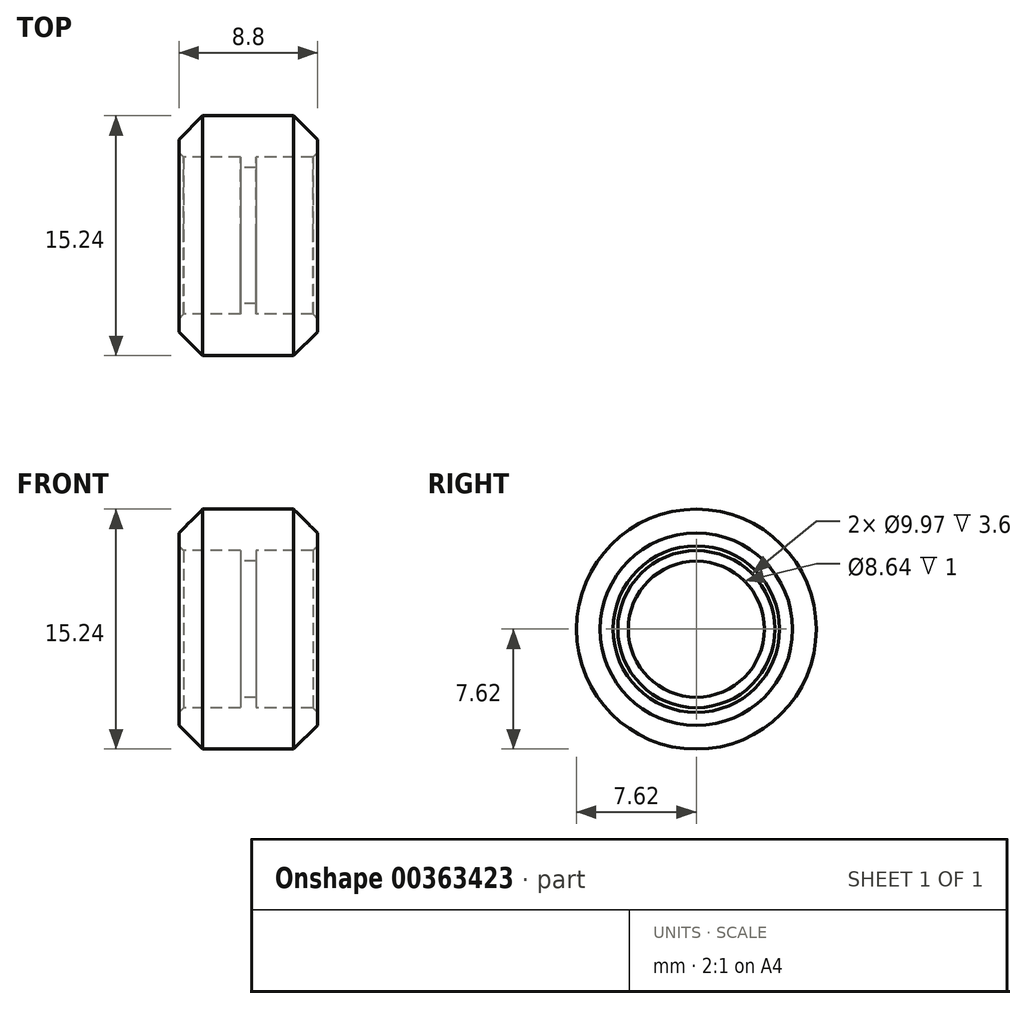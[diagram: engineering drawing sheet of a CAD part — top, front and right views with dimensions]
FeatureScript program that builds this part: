
annotation { "Feature Type Name" : "Feature", "Feature Type Description" : "" }
export const myFeature = defineFeature(function(context is Context, id is Id, definition is map)
    precondition{}
    {
        {
            var Q0;
            Q0=qCreatedBy(makeId("Front.planeOp"),FACE);
            var sketch = newSketch(context, id + "F0", { "sketchPlane" : qUnion([Q0])});
            skLineSegment(sketch, "E0", {"start": v(0.5, 4.32) * mm, "end": v(0.5, 4.99) * mm});
            skLineSegment(sketch, "E1", {"start": v(0.5, 4.99) * mm, "end": v(4.1, 4.99) * mm});
            skLineSegment(sketch, "E2", {"start": v(4.4, 5.29) * mm, "end": v(4.4, 6.1) * mm});
            skLineSegment(sketch, "E3", {"start": v(4.4, 6.1) * mm, "end": v(2.89, 7.62) * mm});
            skLineSegment(sketch, "E4", {"start": v(2.9, 7.62) * mm, "end": v(-2.9, 7.62) * mm});
            skLineSegment(sketch, "E5", {"start": v(-2.9, 7.62) * mm, "end": v(-4.4, 6.1) * mm});
            skLineSegment(sketch, "E6", {"start": v(-4.4, 6.1) * mm, "end": v(-4.4, 5.29) * mm});
            skLineSegment(sketch, "E7", {"start": v(-4.1, 4.99) * mm, "end": v(-0.5, 4.99) * mm});
            skLineSegment(sketch, "E8", {"start": v(-0.5, 4.99) * mm, "end": v(-0.5, 4.32) * mm});
            skPoint(sketch, "E9", {"position": v(0, 7.62) * mm});
            skLineSegment(sketch, "E10", {"start": v(-0.5, 4.32) * mm, "end": v(0.5, 4.32) * mm});
            skPoint(sketch, "E11", {"position": v(0, 4.32) * mm});
            skPoint(sketch, "E12", {"position": v(-4.4, 5.29) * mm});
            skPoint(sketch, "E13", {"position": v(-4.1, 4.99) * mm});
            skPoint(sketch, "E14", {"position": v(4.1, 4.99) * mm});
            skPoint(sketch, "E15", {"position": v(4.4, 5.29) * mm});
            skLineSegment(sketch, "E16", {"start": v(-4.4, 5.29) * mm, "end": v(-4.1, 4.99) * mm});
            skLineSegment(sketch, "E17", {"start": v(4.4, 5.29) * mm, "end": v(4.1, 4.99) * mm});
            skPoint(sketch, "E18.orphan", {"position": v(-4.4, 4.99) * mm});
            skPoint(sketch, "E19.orphan", {"position": v(4.4, 4.99) * mm});
            skLineSegment(sketch, "E20", {"start": v(-12.77, 0) * mm, "end": v(10.11, 0) * mm, "construction": true});
            skSolve(sketch);
        }
        {
            var Q0;
            Q0=makeQuery(id+"F0.imprint","IMPRINT",FACE,{"disambiguationData":[TD([[makeQuery(id+"F0.imprint","IMPRINT",EDGE,{"derivedFrom":sQuery(id+"F0.wireOp",EDGE,"E0")}),1.0]])]});
            var Q1;
            Q1=sQuery(id+"F0.wireOp",EDGE,"E20");
            revolve(context, id + "F1", {"entities" : qUnion([Q0]), "axis" : qUnion([Q1]), "revolveType" : RevolveType.FULL});
        }
    });
